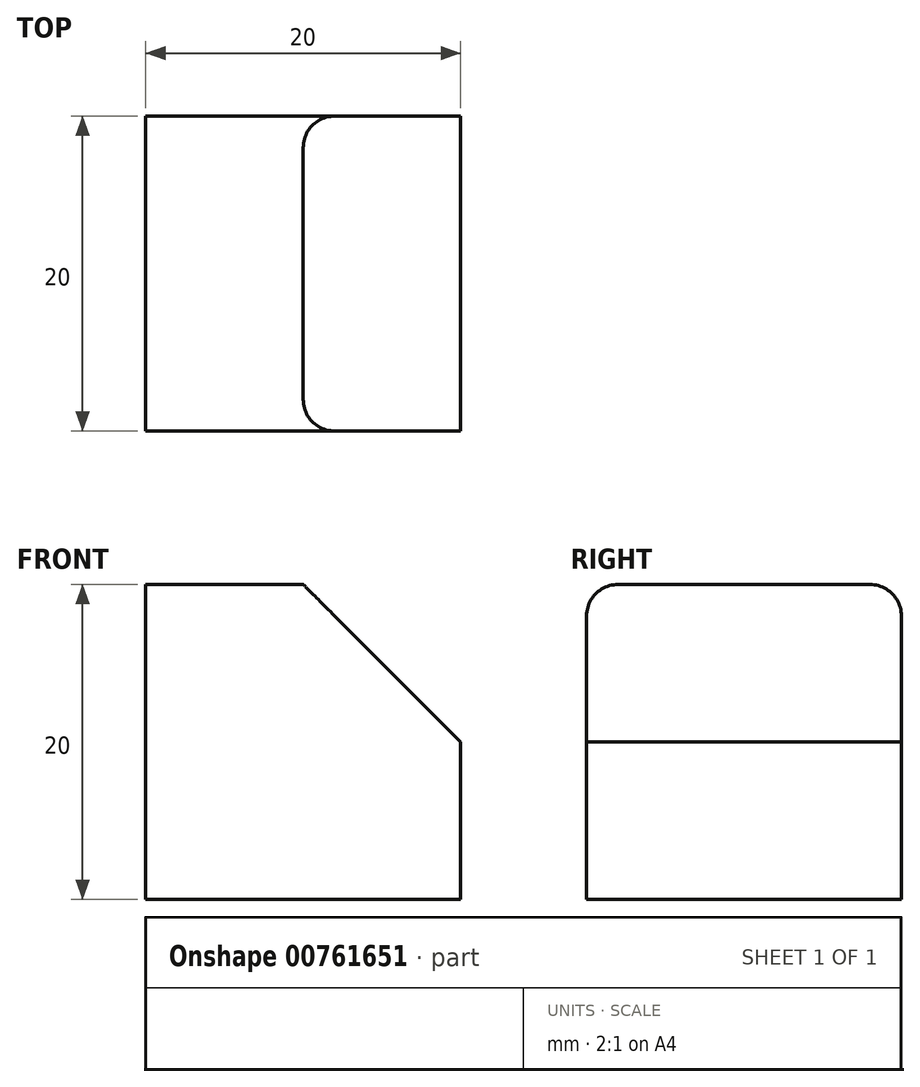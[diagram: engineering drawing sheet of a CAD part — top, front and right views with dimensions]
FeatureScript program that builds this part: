
annotation { "Feature Type Name" : "Feature", "Feature Type Description" : "" }
export const myFeature = defineFeature(function(context is Context, id is Id, definition is map)
    precondition{}
    {
        {
            var Q0;
            Q0=qCreatedBy(makeId("Front.planeOp"),FACE);
            var sketch = newSketch(context, id + "F0", { "sketchPlane" : qUnion([Q0])});
            skLineSegment(sketch, "E0", {"start": v(0.77, -9.45) * mm, "end": v(-19.23, -9.45) * mm});
            skLineSegment(sketch, "E1", {"start": v(-19.23, -9.45) * mm, "end": v(-19.23, 10.55) * mm});
            skLineSegment(sketch, "E2", {"start": v(-19.23, 10.55) * mm, "end": v(-9.23, 10.55) * mm});
            skLineSegment(sketch, "E3", {"start": v(-9.23, 10.55) * mm, "end": v(0.77, 0.55) * mm});
            skLineSegment(sketch, "E4", {"start": v(0.77, 0.55) * mm, "end": v(0.77, -9.45) * mm});
            skSolve(sketch);
        }
        {
            var Q0;
            Q0=makeQuery(id+"F0.imprint","IMPRINT",FACE,{"disambiguationData":[TD([[makeQuery(id+"F0.imprint","IMPRINT",EDGE,{"derivedFrom":sQuery(id+"F0.wireOp",EDGE,"E0")}),-1.0]])]});
            extrude(context, id + "F1", {"entities" : qUnion([Q0]), "depth" : 20 * mm, "offsetDistance" : 25 * mm});
        }
        {
            var Q0;
            Q0=makeQuery(id+"F1.opExtrude","CAP_EDGE",EDGE,{"disambiguationData":[OSD([sQuery(id+"F0.wireOp",EDGE,"E2")])],"isStart":true});
            var Q1;
            Q1=makeQuery(id+"F1.opExtrude","CAP_EDGE",EDGE,{"disambiguationData":[OSD([sQuery(id+"F0.wireOp",EDGE,"E2")])],"isStart":false});
            fillet(context, id + "F2", {"entities" : qUnion([Q0, Q1]), "radius" : 2 * mm, "tangentPropagation" : true, "allowEdgeOverflow" : false});
        }
    });
